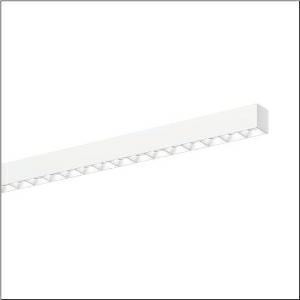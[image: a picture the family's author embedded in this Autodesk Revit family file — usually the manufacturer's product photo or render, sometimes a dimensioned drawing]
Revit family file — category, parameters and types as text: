
# Revit family: silica_r__21_51mx26db35wb_1250
name_source: partatom
category: Lighting Fixtures
units: mm (PartAtom-declared; Revit-internal decimal feet)

## family parameters
Cut with Voids When Loaded = No
Host = Face
Light Source = No
Part Type = Normal
Room Calculation Point = No
Round Connector Dimension = Use Diameter
Shared = No

## types (1)
- --- (1 x LED, 5400 lm, 31.4 W, 3000K)
    Apparent Load = 31 VA
    CIE Flux Codes = 83 98 100 100 100
    Color Rendering = 80
    Color Temperature = 3000K
    Default Elevation = 1800 mm
    Description = Silica® 21, office luminaire, primary light control with darklight reflector, of PMMA, white, CAT 2 (L<= 3000cd/m²), light emission: direct distribution, primary light characteristic: symmetric, installation type: surface-mounted, LED, rated luminous flux: 5.400lm, luminous efficacy: 172lm/W, light colour: 830, colour temperature: 3000K, control gear: DALI 2, with terminal, 3+2-pole, max. 2.5mm², mains connection: 220..240V, AC, 50/60Hz, rated input power: 31.4W, luminaire housing, of aluminium, traffic white (RAL 9016), length: 1.504mm, width: 53mm, height: 53mm, protection rating (complete): IP20, insulation class (complete): insulation class I (protective earthing), certification: CE, permissible operating ambient temperature: 0..+35°C, standard: EN 50419, packaging unit: 1 piece
    Height = 53 mm
    Lamp = 1 x LED
    Lamp Light Flux = 5400 lm
    Lamp Power = 31.4 W
    Lamp count = 1
    Length = 1504 mm
    Luminous efficacy = 172 lm/W
    Manufacturer = Siteco
    ModVariant = No
    Model = 51MX26DB35WB
    Mounting Place = Ceiling
    Mounting Type = Surface mounted
    Number of Poles = 1
    OnlyDefault = Yes
    Power Factor = 1
    Product Name = Silica® 21
    Product group = office luminaire | ceiling mounted
    ProductGroupID = 302
    Protection Class = Protection class I
    Protection Degree = IP 20
    RLX_Detail_Level = 1
    RLX_Emergency_Light_Flux = 0 lm
    RLX_Emergency_Type = 0
    RLX_Emergency_Type_DB = No
    RlxData = <blob elided: 41733 chars, md5=1dc9ea76>
    Socket = socket
    Standby Power = 0 W
    System Light Flux = 5400 lm
    System Power = 31 W
    Type Comments = factory setting: luminous flux: 100 % | dim-lin: 254 | 360 mA
    Type Image = l_1335934.jpg
    URL = http://relux.com
    VarID = @adj_124252
    Voltage = 0 V
    Weight = 0.00 kg
    Width = 53 mm

## geometry (parser evidence)
native form markers: Blend x4, Sweep x12
no freeform markers — native parametric forms only
